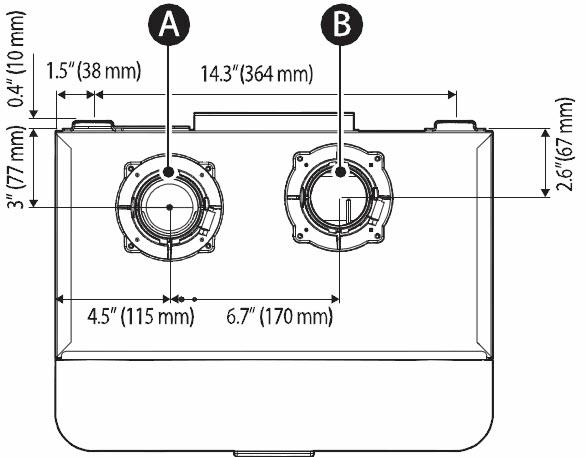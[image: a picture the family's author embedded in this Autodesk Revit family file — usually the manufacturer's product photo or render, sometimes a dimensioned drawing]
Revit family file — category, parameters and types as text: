
# Revit family: Water_Heater-Racks-Navien-NPE-9_Unit_Front-Wall-02
name_source: partatom
category: Mechanical Equipment
revit_build: Autodesk Revit 2016 (Build: 20150220_1215(x64)
units: mm (PartAtom-declared; Revit-internal decimal feet)

## family parameters
Cut with Voids When Loaded = No
Host = Face
OmniClass Number = 23.65.35.11
OmniClass Title = Supply Water Heaters
Part Type = Normal
Room Calculation Point = No
Round Connector Dimension = Use Diameter
Shared = No

## types (4) — shared parameters
2" Exhaust/Intake = Yes
3" Exhaust/Intake = No
Apparent Load = 0 VA
Assembly Code = D3010500
Certifications = Energy Star | AHRI | CSA | CSA | NFS
Cold Water Inlet = 1"
Configuration = NPE_F9_3F2F_4F
Default Elevation = 48 "
Depth = 23.8 "
Description = 9 Unit Front
Exhaust = 2"
Finish = Metal - Navien - White
Flow Rate = 1 GPM
Flow Rate Note = 35°F (19°C) temp rise: 11.2 GPM (42 L/m) | 45°F (25°C) temp rise: 8.7 GPM (33 L/m) | 67°F (36°C) temp rise: NPE-240A: 5.6 GPM(21 L/m), NPE-240S: 5.7 GPM(22 L/m)
Frequency = 60 Hz
Gas Inlet = 1"
Heating Capacity = 120000.0 Btu/h
Heating Capacity Note = 19,900–199,900 (BTU/H)
Height = 65.5 "
Hot Water Outlet = 1"
Ignition = Electronic ignition
Installation Type = Indoor
Intake = 2"
Keynote = 22 33 00.A1
Manifold(s) = (1) 30019040A + (1) 30019041A + (1) 30019043A
Manufacturer = Navien, Inc.
Manufacturer Fax Number = (949) 420-0430
Natural Gas Manifold Pressure = -0.05" WC to -0.58" WC
Natural Gas Supply Pressure = 3.5"–10.5" WC
Number of Poles = 1
Phase = 1
Power Factor = 1
Product Documentation Link = https://www.navieninc.com
Product Name = NPE Series Tankless Water Heaters w/ Racks
Product Page URL = https://www.navieninc.com
Propane Gas Manifold Pressure = -0.10" WC to -0.78" WC
Propane Gas Supply Pressure = 8"–13" WC
Required Cascade Operation Accessory = (9) 30014367A (Common Vent Damper & Cascade Communication Cable) or (8) GXXX000546 (Individual Vent Cascade Communication Cable)
URL = https://www.navieninc.com
Venting = Exhaust: 2" PVC, CPVC, PP, SS / 2" special gas vent type BH (Class II, A/B/C) | Intake: 2" PVC, CPVC, PP, SS / 2" special gas vent type BH (Class II, A/B/C) | Vent clearances: 0" to combustibles
Venting Type = Forced draft direct vent
Version = 2016 - v1.0.a
Voltage = 120 V
Water Pressure = 15–150 PSI
Wi-Fi Ready = NaviLink Wi-Fi Control: PBCM-AS-001
Width = 23.3 "

## per-type parameters (varying)
| type | Constraints | Model | Natural Gas | Propane Gas | Recirculation Inlet | Recirculation Inlet Visibility | Tankless Water Heaters | Weight |
| Natural Gas - Recirculating System - NPE-240A(Advanced)-NG | 6 | (9) NPE-240A-NG | Yes | No | 0" | Yes | (9) NPE-240A-NG | 82.00 lbf |
| Natural Gas - NPE-240S(Standard)-NG | 7 | (9) NPE-240S-NG | Yes | No | 1" | No | (9) NPE-240S-NG | 75.00 lbf |
| Propane Gas - Recirculating System - NPE-240A(Advanced)-LPG | 6 | (9) NPE-240A-LPG | No | Yes | 0" | Yes | (9) NPE-240A-LPG | 82.00 lbf |
| Propane Gas - NPE-240S(Standard)-LPG | 7 | (9) NPE-240S-LPG | No | Yes | 1" | No | (9) NPE-240S-LPG | 75.00 lbf |

## geometry (parser evidence)
native form markers: Sweep x11
no freeform markers — native parametric forms only
